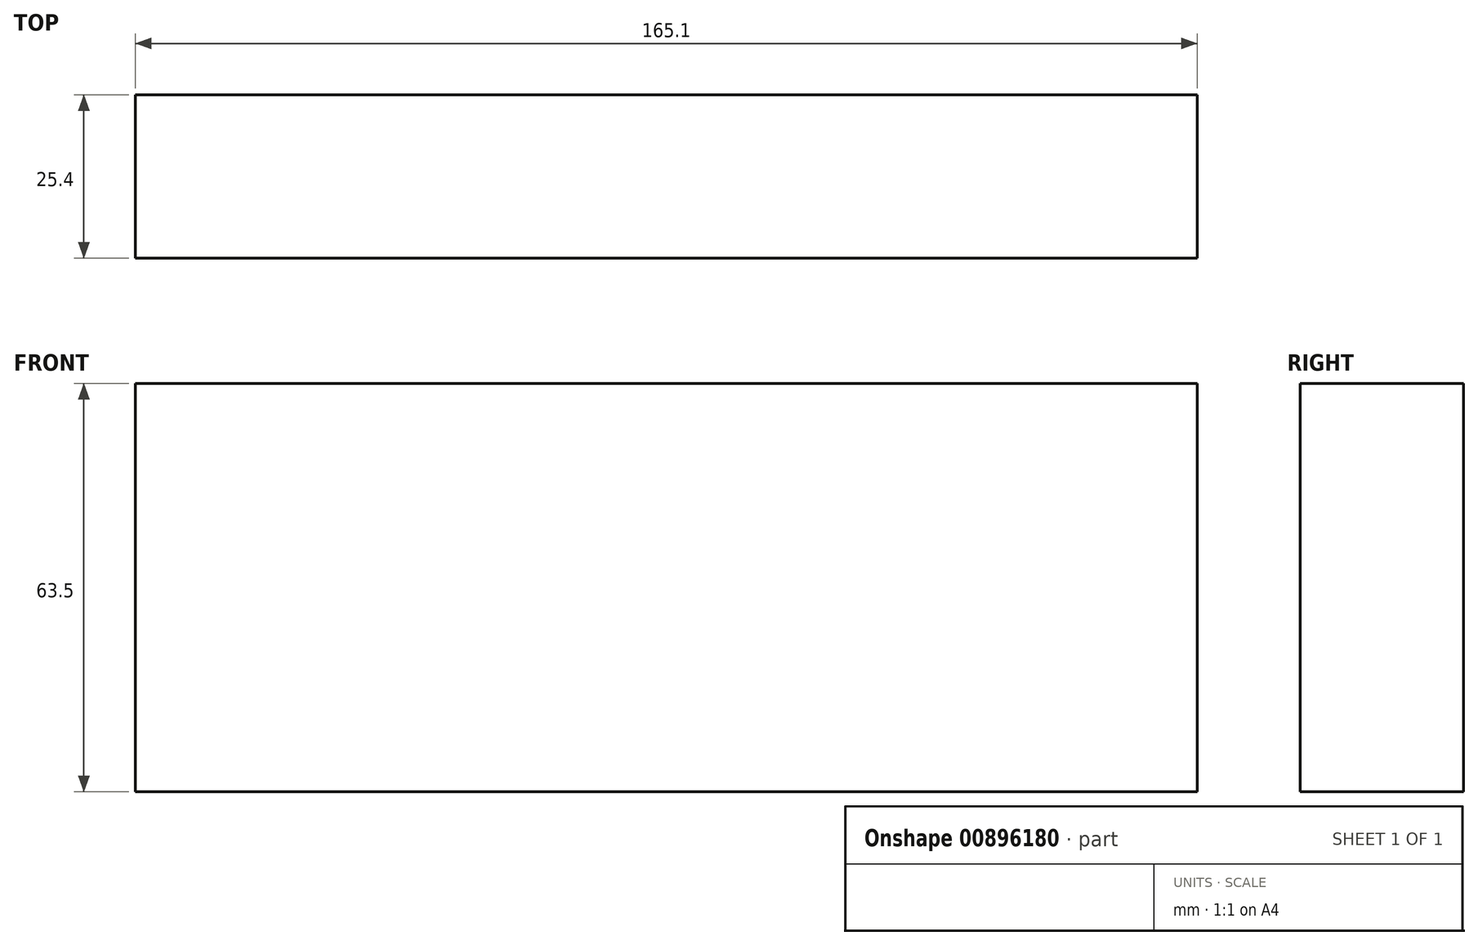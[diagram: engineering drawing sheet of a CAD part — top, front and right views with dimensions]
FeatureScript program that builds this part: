
annotation { "Feature Type Name" : "Feature", "Feature Type Description" : "" }
export const myFeature = defineFeature(function(context is Context, id is Id, definition is map)
    precondition{}
    {
        {
            var Q0;
            Q0=qCreatedBy(makeId("Front.planeOp"),FACE);
            var sketch = newSketch(context, id + "F0", { "sketchPlane" : qUnion([Q0])});
            skLineSegment(sketch, "E0.bottom", {"start": v(0, 0) * mm, "end": v(165.1, 0) * mm});
            skLineSegment(sketch, "E0.top", {"start": v(0, -63.5) * mm, "end": v(165.1, -63.5) * mm});
            skLineSegment(sketch, "E0.left", {"start": v(0, 0) * mm, "end": v(0, -63.5) * mm});
            skLineSegment(sketch, "E0.right", {"start": v(165.1, 0) * mm, "end": v(165.1, -63.5) * mm});
            skSolve(sketch);
        }
        {
            var Q0;
            Q0=makeQuery(id+"F0.imprint","IMPRINT",FACE,{"disambiguationData":[TD([[makeQuery(id+"F0.imprint","IMPRINT",EDGE,{"derivedFrom":sQuery(id+"F0.wireOp",EDGE,"E0.bottom")}),-1.0]])]});
            extrude(context, id + "F1", {"entities" : qUnion([Q0]), "depth" : 25.4 * mm, "offsetDistance" : 25.4 * mm});
        }
    });
